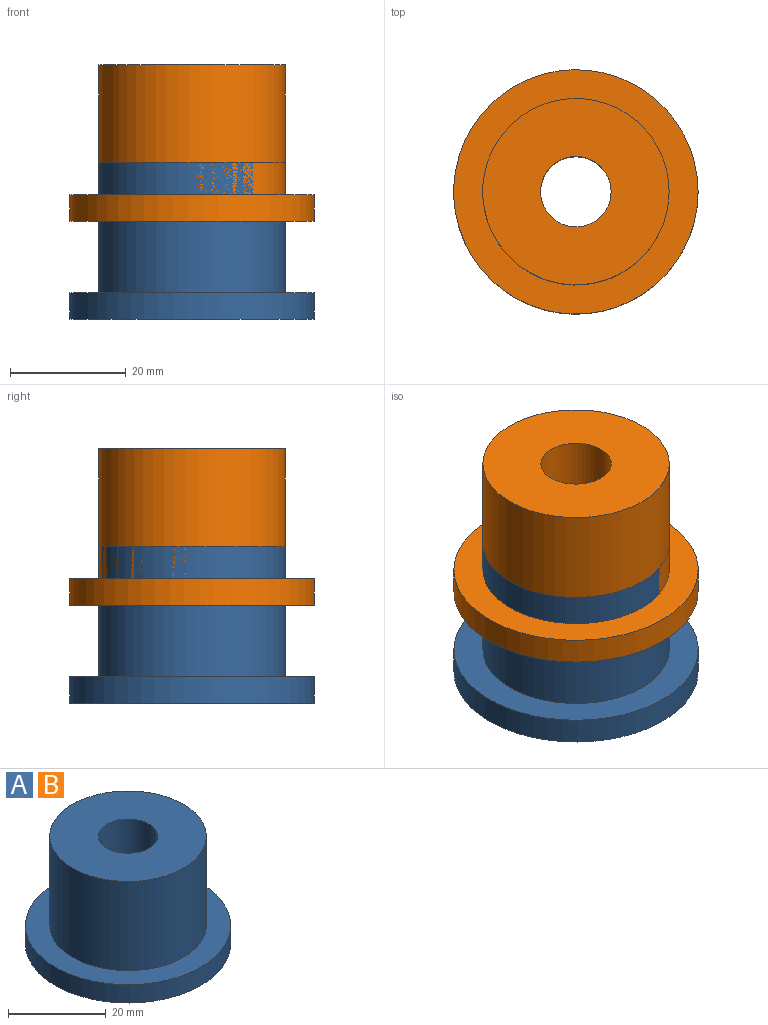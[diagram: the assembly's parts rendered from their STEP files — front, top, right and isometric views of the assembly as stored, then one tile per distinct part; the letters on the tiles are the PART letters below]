
ASSEMBLY  parts=2 mates=2
PART A: 6 faces, bbox 42.2x42.2x27 mm
  f0: cylinder r=21.08mm len=42.15mm, axis (0,0,-1), area 609.1mm2, adj f1,f2
  f1: plane 42.15x42.15mm, normal (0,0,1), area 583.6mm2, adj f0,f4
  f2: plane 42.15x42.15mm, normal (0,0,-1), area 1279.4mm2, adj f0,f3
  f3: cylinder r=6.08mm len=27mm, axis (0,0,-1), area 1030.7mm2, adj f2,f5
  f4: cylinder r=16.08mm len=32.15mm, axis (0,0,-1), area 2262.5mm2, adj f1,f5
  f5: plane 32.15x32.15mm, normal (0,0,1), area 695.9mm2, adj f3,f4
PART B: same geometry as A
PLACE A rot(axis=(0.23,0.76,-0.6),0deg) t=(6.96,0.23,1.39)mm
PLACE B t=(6.96,0.23,18.27)mm
MATE slider B.f0 <-> A.f0  axis (0,0,1) through (50.82,10.52,45.27)mm
MATE parallel B.f0 <-> A.f0  axis (0,0,-1) through (50.82,10.52,18.27)mm
